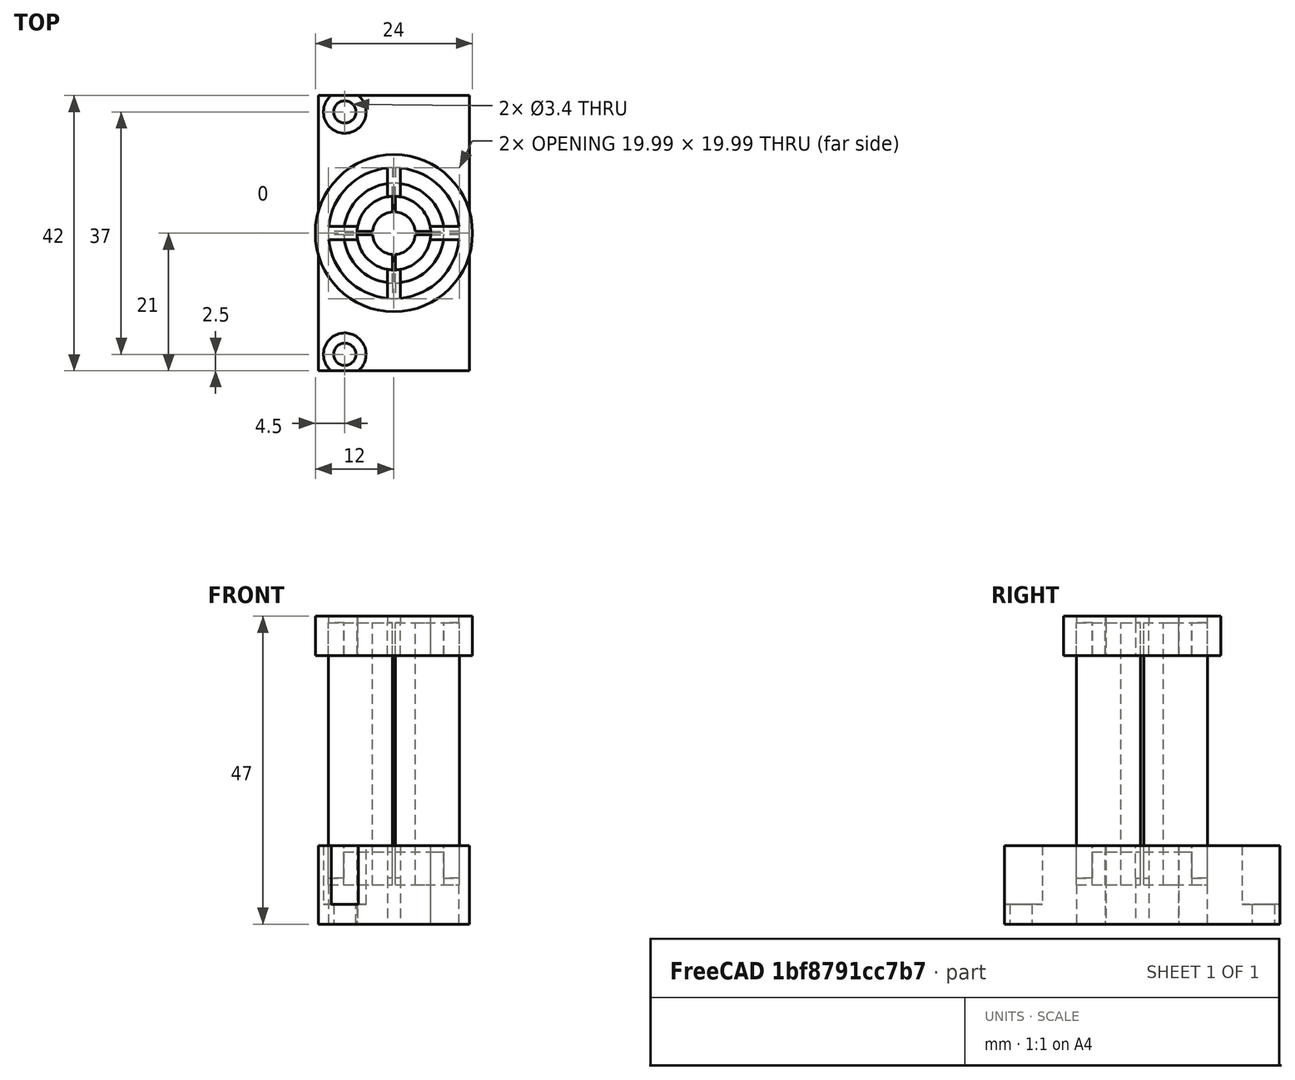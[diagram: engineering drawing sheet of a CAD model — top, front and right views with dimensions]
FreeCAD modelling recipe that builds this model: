
FCSTD DOCUMENT  (FreeCAD 1.0R1.0.0)
Label: Quak_XL30_Modulator3
License: All rights reserved
LicenseURL: http://en.wikipedia.org/wiki/All_rights_reserved
objects: Part::Cut×18, Part::FeaturePython×11, Part::Box×11, TechDraw::DrawViewDimension×9, Part::MultiFuse×8, Part::Cylinder×7, Part::Compound×5, TechDraw::DrawProjGroupItem×3, App::Link×1, Spreadsheet::Sheet×1, TechDraw::DrawSVGTemplate×1, TechDraw::DrawViewSection×1, TechDraw::DrawPage×1
note: 71 computed .brp shape members not serialized (recipe doc carries the construction recipe); baked Part::Feature solids carry a one-line shape summary decoded from their .brp
EXTERNAL_REF file=XL30ColumnAttachmentRing_PCBKicker01.FCStd obj=Cut007

FEATURE [App::Link] Link  label="Stackmountring02"
  LinkedObject = -> <external XL30ColumnAttachmentRing_PCBKicker01.FCStd>#Cut007
FEATURE [Part::FeaturePython] Tube  # WARN: FeaturePython — macro-defined, semantics opaque (R4)
  AttacherType = Attacher::AttachEngine3D
  Height = 40
  InnerRadius = 3.25
  OuterRadius = 10
  expr: Height = <<Modulator3>>.kicker_length
  expr: InnerRadius = <<Modulator3>>.beamhole_diameter / 2
  expr: OuterRadius = <<Modulator3>>.outer_dia / 2
FEATURE [Spreadsheet::Sheet] Spreadsheet  label="Modulator3"
  cells = A2='Beamhole diameter; B2(beamhole_diameter)=6.5; A3='Insulation spacing; B3(insulation_spacing)=0.5; A4='Kicker length; B4(kicker_length)=40; A5='Outer diameter; B5(outer_dia)=20; A6='Shielding plate thickness; B6(shield_thickness)=1; A7='Kicker plate offset; B7(kicker_plate_offset)=7; A8='Mountring diameter; B8(mountring_dia)=2; A9='Mountring depth; B9(mountring_depth)=5; A10='PLA mount (pressfit); A11='Thickness; B11(mount_thickness_bottom)=5; A12='Thickness top; B12(mount_thickness_top)=2
FEATURE [Part::Box] Box  label="Cube"
  AttacherType = Attacher::AttachEngine3D
  Height = 40
  Length = 20
  Placement = pos=(-10,-0.25,0) rot=(0,0,1;0rad)
  Width = 0.5
  expr: .Placement.Base.x = -<<Modulator3>>.outer_dia / 2
  expr: .Placement.Base.y = -<<Modulator3>>.insulation_spacing / 2
  expr: Height = <<Modulator3>>.kicker_length
  expr: Length = <<Modulator3>>.outer_dia
  expr: Width = <<Modulator3>>.insulation_spacing
FEATURE [Part::Box] Box001  label="Cube001"
  AttacherType = Attacher::AttachEngine3D
  Height = 40
  Length = 20
  Placement = pos=(-10,-0.25,0) rot=(0,0,1;0rad)
  Width = 0.5
  expr: .Placement.Base.x = -<<Modulator3>>.outer_dia / 2
  expr: .Placement.Base.y = -<<Modulator3>>.insulation_spacing / 2
  expr: Height = <<Modulator3>>.kicker_length
  expr: Length = <<Modulator3>>.outer_dia
  expr: Width = <<Modulator3>>.insulation_spacing
FEATURE [Part::Compound] Compound
  Links = -> [Box001]
  Placement = pos=(0,0,0) rot=(0,0,1;1.5708rad)
FEATURE [Part::MultiFuse] Fusion
  Shapes = -> [Compound,Box]
FEATURE [Part::Cut] Cut
  Base = -> Tube
  Tool = -> Fusion
FEATURE [Part::FeaturePython] Tube001  label="MountringGroove"  # WARN: FeaturePython — macro-defined, semantics opaque (R4)
  AttacherType = Attacher::AttachEngine3D
  Height = 5
  InnerRadius = 5.625
  OuterRadius = 7.625
  expr: Height = <<Modulator3>>.mountring_depth
  expr: InnerRadius = (<<Modulator3>>.beamhole_diameter + <<Modulator3>>.outer_dia) / 4 - <<Modulator3>>.mountring_dia / 2
  expr: OuterRadius = (<<Modulator3>>.beamhole_diameter + <<Modulator3>>.outer_dia) / 4 + <<Modulator3>>.mountring_dia / 2
FEATURE [Part::Cut] Cut001
  Base = -> Cut
  Tool = -> Tube001
FEATURE [Part::FeaturePython] Tube002  label="MountringGroove001"  # WARN: FeaturePython — macro-defined, semantics opaque (R4)
  AttacherType = Attacher::AttachEngine3D
  Height = 5
  InnerRadius = 5.625
  OuterRadius = 7.625
  Placement = pos=(0,0,35) rot=(0,0,1;0rad)
  expr: .Placement.Base.z = <<Modulator3>>.kicker_length - <<Modulator3>>.mountring_depth
  expr: Height = <<Modulator3>>.mountring_depth
  expr: InnerRadius = (<<Modulator3>>.beamhole_diameter + <<Modulator3>>.outer_dia) / 4 - <<Modulator3>>.mountring_dia / 2
  expr: OuterRadius = (<<Modulator3>>.beamhole_diameter + <<Modulator3>>.outer_dia) / 4 + <<Modulator3>>.mountring_dia / 2
FEATURE [Part::Cut] Cut002  label="ModulatorPlates"
  Base = -> Cut001
  Placement = pos=(0,0,11) rot=(0,0,1;0rad)
  Tool = -> Tube002
FEATURE [Part::Box] Box002  label="Cube002"
  AttacherType = Attacher::AttachEngine3D
  Height = 12
  Length = 23
  Placement = pos=(-11.5,-21,0) rot=(0,0,1;0rad)
  Width = 42
  expr: Height = <<Modulator3>>.mount_thickness_bottom + 7
FEATURE [Part::Cylinder] Cylinder
  Angle = 360
  AttacherType = Attacher::AttachEngine3D
  FirstAngle = 0
  Height = 100
  Radius = 5.625
  SecondAngle = 0
  expr: Radius = (<<Modulator3>>.beamhole_diameter + <<Modulator3>>.outer_dia) / 4 - <<Modulator3>>.mountring_dia / 2
FEATURE [Part::Cut] Cut003
  Base = -> Box002
  Tool = -> Cylinder
FEATURE [Part::Box] Box003  label="Cube003"
  AttacherType = Attacher::AttachEngine3D
  Height = 40
  Length = 20
  Placement = pos=(-10,-0.25,0) rot=(0,0,1;0rad)
  Width = 0.5
  expr: .Placement.Base.x = -<<Modulator3>>.outer_dia / 2
  expr: .Placement.Base.y = -<<Modulator3>>.insulation_spacing / 2
  expr: Height = <<Modulator3>>.kicker_length
  expr: Length = <<Modulator3>>.outer_dia
  expr: Width = <<Modulator3>>.insulation_spacing
FEATURE [Part::Box] Box004  label="Cube004"
  AttacherType = Attacher::AttachEngine3D
  Height = 40
  Length = 20
  Placement = pos=(-10,-0.25,0) rot=(0,0,1;0rad)
  Width = 0.5
  expr: .Placement.Base.x = -<<Modulator3>>.outer_dia / 2
  expr: .Placement.Base.y = -<<Modulator3>>.insulation_spacing / 2
  expr: Height = <<Modulator3>>.kicker_length
  expr: Length = <<Modulator3>>.outer_dia
  expr: Width = <<Modulator3>>.insulation_spacing
FEATURE [Part::Compound] Compound001
  Links = -> [Box004]
  Placement = pos=(0,0,0) rot=(0,0,1;1.5708rad)
FEATURE [Part::MultiFuse] Fusion001
  Shapes = -> [Compound001,Box003]
FEATURE [Part::FeaturePython] Tube003  # WARN: FeaturePython — macro-defined, semantics opaque (R4)
  AttacherType = Attacher::AttachEngine3D
  Height = 40
  InnerRadius = 3.25
  OuterRadius = 10
  expr: Height = <<Modulator3>>.kicker_length
  expr: InnerRadius = <<Modulator3>>.beamhole_diameter / 2
  expr: OuterRadius = <<Modulator3>>.outer_dia / 2
FEATURE [Part::Cut] Cut004
  Base = -> Tube003
  Tool = -> Fusion001
FEATURE [Part::FeaturePython] Tube004  label="MountringGroove002"  # WARN: FeaturePython — macro-defined, semantics opaque (R4)
  AttacherType = Attacher::AttachEngine3D
  Height = 5
  InnerRadius = 5.625
  OuterRadius = 7.625
  expr: Height = <<Modulator3>>.mountring_depth
  expr: InnerRadius = (<<Modulator3>>.beamhole_diameter + <<Modulator3>>.outer_dia) / 4 - <<Modulator3>>.mountring_dia / 2
  expr: OuterRadius = (<<Modulator3>>.beamhole_diameter + <<Modulator3>>.outer_dia) / 4 + <<Modulator3>>.mountring_dia / 2
FEATURE [Part::Cut] Cut005
  Base = -> Cut004
  Tool = -> Tube004
FEATURE [Part::FeaturePython] Tube005  label="MountringGroove003"  # WARN: FeaturePython — macro-defined, semantics opaque (R4)
  AttacherType = Attacher::AttachEngine3D
  Height = 5
  InnerRadius = 5.625
  OuterRadius = 7.625
  Placement = pos=(0,0,35) rot=(0,0,1;0rad)
  expr: .Placement.Base.z = <<Modulator3>>.kicker_length - <<Modulator3>>.mountring_depth
  expr: Height = <<Modulator3>>.mountring_depth
  expr: InnerRadius = (<<Modulator3>>.beamhole_diameter + <<Modulator3>>.outer_dia) / 4 - <<Modulator3>>.mountring_dia / 2
  expr: OuterRadius = (<<Modulator3>>.beamhole_diameter + <<Modulator3>>.outer_dia) / 4 + <<Modulator3>>.mountring_dia / 2
FEATURE [Part::Cut] Cut006
  Base = -> Cut005
  Placement = pos=(0,0,7) rot=(0,0,1;0rad)
  Tool = -> Tube005
FEATURE [Part::Cut] Cut007
  Base = -> Cut003
  Placement = pos=(0,0,1) rot=(0,0,1;0rad)
  Tool = -> Cut006
FEATURE [Part::Cylinder] Cylinder001
  Angle = 360
  AttacherType = Attacher::AttachEngine3D
  FirstAngle = 0
  Height = 6
  Placement = pos=(0,0,42) rot=(0,0,1;0rad)
  Radius = 12
  SecondAngle = 0
  expr: .Placement.Base.z = <<Modulator3>>.kicker_length + 7 - <<Modulator3>>.mountring_depth
  expr: Height = <<Modulator3>>.mountring_depth + 1
  expr: Radius = <<Modulator3>>.outer_dia / 2 + 2
FEATURE [Part::Cylinder] Cylinder002
  Angle = 360
  AttacherType = Attacher::AttachEngine3D
  FirstAngle = 0
  Height = 100
  Radius = 5.625
  SecondAngle = 0
  expr: Radius = (<<Modulator3>>.beamhole_diameter + <<Modulator3>>.outer_dia) / 4 - <<Modulator3>>.mountring_dia / 2
FEATURE [Part::Cut] Cut008
  Base = -> Cylinder001
  Tool = -> Cylinder002
FEATURE [Part::Box] Box005  label="Cube005"
  AttacherType = Attacher::AttachEngine3D
  Height = 40
  Length = 20
  Placement = pos=(-10,-0.25,0) rot=(0,0,1;0rad)
  Width = 0.5
  expr: .Placement.Base.x = -<<Modulator3>>.outer_dia / 2
  expr: .Placement.Base.y = -<<Modulator3>>.insulation_spacing / 2
  expr: Height = <<Modulator3>>.kicker_length
  expr: Length = <<Modulator3>>.outer_dia
  expr: Width = <<Modulator3>>.insulation_spacing
FEATURE [Part::Box] Box006  label="Cube006"
  AttacherType = Attacher::AttachEngine3D
  Height = 40
  Length = 20
  Placement = pos=(-10,-0.25,0) rot=(0,0,1;0rad)
  Width = 0.5
  expr: .Placement.Base.x = -<<Modulator3>>.outer_dia / 2
  expr: .Placement.Base.y = -<<Modulator3>>.insulation_spacing / 2
  expr: Height = <<Modulator3>>.kicker_length
  expr: Length = <<Modulator3>>.outer_dia
  expr: Width = <<Modulator3>>.insulation_spacing
FEATURE [Part::Compound] Compound002
  Links = -> [Box006]
  Placement = pos=(0,0,0) rot=(0,0,1;1.5708rad)
FEATURE [Part::MultiFuse] Fusion002
  Shapes = -> [Compound002,Box005]
FEATURE [Part::FeaturePython] Tube006  # WARN: FeaturePython — macro-defined, semantics opaque (R4)
  AttacherType = Attacher::AttachEngine3D
  Height = 40
  InnerRadius = 3.25
  OuterRadius = 10
  expr: Height = <<Modulator3>>.kicker_length
  expr: InnerRadius = <<Modulator3>>.beamhole_diameter / 2
  expr: OuterRadius = <<Modulator3>>.outer_dia / 2
FEATURE [Part::Cut] Cut009
  Base = -> Tube006
  Tool = -> Fusion002
FEATURE [Part::FeaturePython] Tube007  label="MountringGroove004"  # WARN: FeaturePython — macro-defined, semantics opaque (R4)
  AttacherType = Attacher::AttachEngine3D
  Height = 5
  InnerRadius = 5.625
  OuterRadius = 7.625
  expr: Height = <<Modulator3>>.mountring_depth
  expr: InnerRadius = (<<Modulator3>>.beamhole_diameter + <<Modulator3>>.outer_dia) / 4 - <<Modulator3>>.mountring_dia / 2
  expr: OuterRadius = (<<Modulator3>>.beamhole_diameter + <<Modulator3>>.outer_dia) / 4 + <<Modulator3>>.mountring_dia / 2
FEATURE [Part::Cut] Cut010
  Base = -> Cut009
  Tool = -> Tube007
FEATURE [Part::FeaturePython] Tube008  label="MountringGroove005"  # WARN: FeaturePython — macro-defined, semantics opaque (R4)
  AttacherType = Attacher::AttachEngine3D
  Height = 5
  InnerRadius = 5.625
  OuterRadius = 7.625
  Placement = pos=(0,0,35) rot=(0,0,1;0rad)
  expr: .Placement.Base.z = <<Modulator3>>.kicker_length - <<Modulator3>>.mountring_depth
  expr: Height = <<Modulator3>>.mountring_depth
  expr: InnerRadius = (<<Modulator3>>.beamhole_diameter + <<Modulator3>>.outer_dia) / 4 - <<Modulator3>>.mountring_dia / 2
  expr: OuterRadius = (<<Modulator3>>.beamhole_diameter + <<Modulator3>>.outer_dia) / 4 + <<Modulator3>>.mountring_dia / 2
FEATURE [Part::Cut] Cut011
  Base = -> Cut010
  Placement = pos=(0,0,7) rot=(0,0,1;0rad)
  Tool = -> Tube008
FEATURE [Part::Cut] Cut012  label="mountring_top"
  Base = -> Cut008
  Placement = pos=(0,0,4) rot=(0,0,1;0rad)
  Tool = -> Cut011
FEATURE [Part::Cylinder] Cylinder003
  Angle = 360
  AttacherType = Attacher::AttachEngine3D
  FirstAngle = 0
  Height = 12
  Radius = 1.7
  SecondAngle = 0
  expr: Height = <<Modulator3>>.mount_thickness_bottom + 7
FEATURE [Part::Cylinder] Cylinder004
  Angle = 360
  AttacherType = Attacher::AttachEngine3D
  FirstAngle = 0
  Height = 9
  Placement = pos=(0,0,3) rot=(0,0,1;0rad)
  Radius = 3.25
  SecondAngle = 0
  expr: Height = <<Modulator3>>.mount_thickness_bottom + 7 - 3
  expr: Radius = 3.25 mm
FEATURE [Part::MultiFuse] Fusion003
  Placement = pos=(-7.5,18.5,0) rot=(0,0,1;0rad)
  Shapes = -> [Cylinder004,Cylinder003]
FEATURE [Part::Cylinder] Cylinder005
  Angle = 360
  AttacherType = Attacher::AttachEngine3D
  FirstAngle = 0
  Height = 12
  Radius = 1.7
  SecondAngle = 0
  expr: Height = <<Modulator3>>.mount_thickness_bottom + 7
FEATURE [Part::Cylinder] Cylinder006
  Angle = 360
  AttacherType = Attacher::AttachEngine3D
  FirstAngle = 0
  Height = 9
  Placement = pos=(0,0,3) rot=(0,0,1;0rad)
  Radius = 3.25
  SecondAngle = 0
  expr: Height = <<Modulator3>>.mount_thickness_bottom + 7 - 3
  expr: Radius = 3.25 mm
FEATURE [Part::MultiFuse] Fusion004
  Placement = pos=(-7.5,-18.5,0) rot=(0,0,1;0rad)
  Shapes = -> [Cylinder006,Cylinder005]
  expr: .Placement.Base.y = -18.5 mm
FEATURE [Part::MultiFuse] Fusion005
  Placement = pos=(0,0,1) rot=(0,0,1;0rad)
  Shapes = -> [Fusion004,Fusion003]
FEATURE [Part::Cut] Cut013
  Base = -> Cut007
  Placement = pos=(0,0,4) rot=(0,0,1;0rad)
  Tool = -> Fusion005
FEATURE [Part::Box] Box009  label="Cube009"
  AttacherType = Attacher::AttachEngine3D
  Height = 80
  Length = 20
  Placement = pos=(-10,-1,-20) rot=(0,0,1;0rad)
  Width = 2
  expr: .Placement.Base.x = -<<Modulator3>>.outer_dia / 2
  expr: .Placement.Base.y = -(<<Modulator3>>.insulation_spacing * 4) / 2
  expr: .Placement.Base.z = -<<Modulator3>>.kicker_length / 2
  expr: Height = <<Modulator3>>.kicker_length * 2
  expr: Length = <<Modulator3>>.outer_dia
  expr: Width = <<Modulator3>>.insulation_spacing * 4
FEATURE [Part::Box] Box010  label="Cube010"
  AttacherType = Attacher::AttachEngine3D
  Height = 80
  Length = 20
  Placement = pos=(-10,-1,-20) rot=(0,0,1;0rad)
  Width = 2
  expr: .Placement.Base.x = -<<Modulator3>>.outer_dia / 2
  expr: .Placement.Base.y = -(<<Modulator3>>.insulation_spacing * 4) / 2
  expr: .Placement.Base.z = -<<Modulator3>>.kicker_length / 2
  expr: Height = <<Modulator3>>.kicker_length * 2
  expr: Length = <<Modulator3>>.outer_dia
  expr: Width = <<Modulator3>>.insulation_spacing * 4
FEATURE [Part::Compound] Compound004
  Links = -> [Box010]
  Placement = pos=(0,0,0) rot=(0,0,1;1.5708rad)
FEATURE [Part::MultiFuse] Fusion007
  Shapes = -> [Compound004,Box009]
FEATURE [Part::FeaturePython] Tube012  # WARN: FeaturePython — macro-defined, semantics opaque (R4)
  AttacherType = Attacher::AttachEngine3D
  Height = 80
  InnerRadius = 3.25
  OuterRadius = 10
  Placement = pos=(0,0,-20) rot=(0,0,1;0rad)
  expr: .Placement.Base.z = -<<Modulator3>>.kicker_length / 2
  expr: Height = <<Modulator3>>.kicker_length * 2
  expr: InnerRadius = <<Modulator3>>.beamhole_diameter / 2
  expr: OuterRadius = <<Modulator3>>.outer_dia / 2
FEATURE [Part::Cut] Cut017
  Base = -> Tube012
  Tool = -> Fusion007
FEATURE [Part::Box] Box011  label="Cube011"
  AttacherType = Attacher::AttachEngine3D
  Height = 80
  Length = 20
  Placement = pos=(-10,-1,-20) rot=(0,0,1;0rad)
  Width = 2
  expr: .Placement.Base.x = -<<Modulator3>>.outer_dia / 2
  expr: .Placement.Base.y = -(<<Modulator3>>.insulation_spacing * 4) / 2
  expr: .Placement.Base.z = -<<Modulator3>>.kicker_length / 2
  expr: Height = <<Modulator3>>.kicker_length * 2
  expr: Length = <<Modulator3>>.outer_dia
  expr: Width = <<Modulator3>>.insulation_spacing * 4
FEATURE [Part::Box] Box012  label="Cube012"
  AttacherType = Attacher::AttachEngine3D
  Height = 80
  Length = 20
  Placement = pos=(-10,-1,-20) rot=(0,0,1;0rad)
  Width = 2
  expr: .Placement.Base.x = -<<Modulator3>>.outer_dia / 2
  expr: .Placement.Base.y = -(<<Modulator3>>.insulation_spacing * 4) / 2
  expr: .Placement.Base.z = -<<Modulator3>>.kicker_length / 2
  expr: Height = <<Modulator3>>.kicker_length * 2
  expr: Length = <<Modulator3>>.outer_dia
  expr: Width = <<Modulator3>>.insulation_spacing * 4
FEATURE [Part::Compound] Compound005
  Links = -> [Box012]
  Placement = pos=(0,0,0) rot=(0,0,1;1.5708rad)
FEATURE [Part::MultiFuse] Fusion008
  Shapes = -> [Compound005,Box011]
FEATURE [Part::FeaturePython] Tube013  # WARN: FeaturePython — macro-defined, semantics opaque (R4)
  AttacherType = Attacher::AttachEngine3D
  Height = 80
  InnerRadius = 3.25
  OuterRadius = 10
  Placement = pos=(0,0,-20) rot=(0,0,1;0rad)
  expr: .Placement.Base.z = -<<Modulator3>>.kicker_length / 2
  expr: Height = <<Modulator3>>.kicker_length * 2
  expr: InnerRadius = <<Modulator3>>.beamhole_diameter / 2
  expr: OuterRadius = <<Modulator3>>.outer_dia / 2
FEATURE [Part::Cut] Cut018
  Base = -> Tube013
  Tool = -> Fusion008
FEATURE [Part::Cut] Cut019  label="TopRing"
  Base = -> Cut012
  Tool = -> Cut018
FEATURE [Part::Cut] Cut020  label="BottomMount"
  Base = -> Cut013
  Tool = -> Cut017
FEATURE [TechDraw::DrawSVGTemplate] Template
  EditableTexts = creator=Thomas Spielauer; date_of_issue=2 Apr 2025; document_type=Part Drawing; general_tolerances=ISO 2768-m; identification_number=1; language_code=EN; part_material=Copper; revision_index=1; sheet_number=1 / 1; sheet_scale=1 : 1; title=Circular Modulator Plates
  Height = 210
  Orientation = 1
  Template = <path>
  Width = 297
FEATURE [TechDraw::DrawProjGroupItem] View
  CoarseView = false
  Direction = (0,-1,0)
  Focus = 100
  HardHidden = false
  IsoCount = 0
  IsoHidden = false
  IsoVisible = false
  LockPosition = false
  Perspective = false
  Rotation = 0
  RotationVector = (1,0,0)
  Scale = 2
  ScaleType = 2
  ScrubCount = 1
  SeamHidden = false
  SeamVisible = false
  SmoothHidden = false
  SmoothVisible = true
  Source = -> [Cut002]
  Type = 0
  X = 51.9109
  XDirection = (1,0,0)
  Y = 139.65
FEATURE [TechDraw::DrawProjGroupItem] View001
  CoarseView = false
  Direction = (0,0,1)
  Focus = 100
  HardHidden = false
  IsoCount = 0
  IsoHidden = false
  IsoVisible = false
  LockPosition = false
  Perspective = false
  Rotation = 0
  RotationVector = (1,0,0)
  Scale = 3
  ScaleType = 2
  ScrubCount = 1
  SeamHidden = false
  SeamVisible = false
  SmoothHidden = false
  SmoothVisible = true
  Source = -> [Cut002]
  Type = 0
  X = 116.051
  XDirection = (1,0,0)
  Y = 139.65
FEATURE [TechDraw::DrawViewSection] SectionView  label="Section  - "
  BaseView = -> View001
  CoarseView = false
  CutSurfaceDisplay = 2
  Direction = (-1,-1e-16,0)
  FileGeomPattern = <path>
  FileHatchPattern = <path>
  Focus = 100
  FuseBeforeCut = false
  HardHidden = false
  HatchOffset = (0,0,0)
  HatchRotation = 0
  HatchScale = 1
  IsoCount = 0
  IsoHidden = false
  IsoVisible = false
  LockPosition = false
  NameGeomPattern = Diamond
  Perspective = false
  Rotation = -90
  Scale = 3
  ScaleType = 2
  ScrubCount = 1
  SeamHidden = false
  SeamVisible = false
  SectionDirection = 4
  SectionLineStretch = 1
  SectionNormal = (-1,-1e-16,0)
  SectionOrigin = (0,0,31)
  SmoothHidden = false
  SmoothVisible = true
  Source = -> [Cut002]
  TrimAfterCut = false
  UsePreviousCut = false
  X = 219.773
  XDirection = (1e-16,-1,0)
  Y = 139.65
FEATURE [TechDraw::DrawProjGroupItem] View002
  CoarseView = false
  Direction = (-0.57735,0.57735,0.57735)
  Focus = 100
  HardHidden = false
  IsoCount = 0
  IsoHidden = false
  IsoVisible = false
  LockPosition = false
  Perspective = false
  Rotation = 0
  RotationVector = (1,0,0)
  ScaleType = 0
  ScrubCount = 1
  SeamHidden = false
  SeamVisible = false
  SmoothHidden = false
  SmoothVisible = true
  Source = -> [Cut002]
  Type = 0
  X = 58.6848
  XDirection = (-0.816496,-0.408248,-0.408248)
  Y = 44.7369
FEATURE [TechDraw::DrawViewDimension] Dimension
  AngleOverride = false
  Arbitrary = false
  ArbitraryTolerances = false
  BoxCorners = (2) [(-19.9937,-40,-1e-07),(19.9937,40,1e-07)]
  EqualTolerance = true
  ExtensionAngle = 0
  FormatSpec = %.2w
  FormatSpecOverTolerance = %+.2w
  FormatSpecUnderTolerance = %+.2w
  Inverted = false
  LineAngle = 0
  LockPosition = false
  MeasureType = 1
  OverTolerance = 0
  References2D = -> [View]
  Rotation = 0
  ScaleType = 0
  TheoreticalExact = false
  Type = 2
  UnderTolerance = 0
  X = -28.5041
  Y = 5.24359
FEATURE [TechDraw::DrawViewDimension] Dimension001
  AngleOverride = false
  Arbitrary = false
  ArbitraryTolerances = false
  BoxCorners = (2) [(-29.9906,-29.9906,0),(29.9906,29.9906,0)]
  EqualTolerance = true
  ExtensionAngle = 0
  FormatSpec = ⌀%.2w
  FormatSpecOverTolerance = %+.2w
  FormatSpecUnderTolerance = %+.2w
  Inverted = false
  LineAngle = 0
  LockPosition = false
  MeasureType = 1
  OverTolerance = 0
  References2D = -> [View001]
  Rotation = 0
  ScaleType = 0
  TheoreticalExact = false
  Type = 5
  UnderTolerance = 0
  X = -33.5321
  Y = 32.1098
FEATURE [TechDraw::DrawViewDimension] Dimension002
  AngleOverride = false
  Arbitrary = false
  ArbitraryTolerances = false
  BoxCorners = (2) [(-29.9906,-29.9906,0),(29.9906,29.9906,0)]
  EqualTolerance = true
  ExtensionAngle = 0
  FormatSpec = ⌀%.2w
  FormatSpecOverTolerance = %+.2w
  FormatSpecUnderTolerance = %+.2w
  Inverted = false
  LineAngle = 0
  LockPosition = false
  MeasureType = 1
  OverTolerance = 0
  References2D = -> [View001]
  Rotation = 0
  ScaleType = 0
  TheoreticalExact = false
  Type = 5
  UnderTolerance = 0
  X = -26.99
  Y = 39.9471
FEATURE [TechDraw::DrawViewDimension] Dimension003
  AngleOverride = false
  Arbitrary = false
  ArbitraryTolerances = false
  BoxCorners = (2) [(-29.9906,-29.9906,0),(29.9906,29.9906,0)]
  EqualTolerance = true
  ExtensionAngle = 0
  FormatSpec = ⌀%.2w
  FormatSpecOverTolerance = %+.2w
  FormatSpecUnderTolerance = %+.2w
  Inverted = false
  LineAngle = 0
  LockPosition = false
  MeasureType = 1
  OverTolerance = 0
  References2D = -> [View001]
  Rotation = 0
  ScaleType = 0
  TheoreticalExact = false
  Type = 5
  UnderTolerance = 0
  X = -19.0316
  Y = 46.4094
FEATURE [TechDraw::DrawViewDimension] Dimension004
  AngleOverride = false
  Arbitrary = false
  ArbitraryTolerances = false
  BoxCorners = (2) [(-29.9906,-29.9906,0),(29.9906,29.9906,0)]
  EqualTolerance = true
  ExtensionAngle = 0
  FormatSpec = ⌀%.2w
  FormatSpecOverTolerance = %+.2w
  FormatSpecUnderTolerance = %+.2w
  Inverted = false
  LineAngle = 0
  LockPosition = false
  MeasureType = 1
  OverTolerance = 0
  References2D = -> [View001]
  Rotation = 0
  ScaleType = 0
  TheoreticalExact = false
  Type = 5
  UnderTolerance = 0
  X = -9.58678
  Y = 48.0562
FEATURE [TechDraw::DrawViewDimension] Dimension005
  AngleOverride = false
  Arbitrary = false
  ArbitraryTolerances = false
  BoxCorners = (2) [(-60,-29.9906,-1e-07),(60,29.9906,1e-07)]
  EqualTolerance = true
  ExtensionAngle = 0
  FormatSpec = %.2w
  FormatSpecOverTolerance = %+.2w
  FormatSpecUnderTolerance = %+.2w
  Inverted = false
  LineAngle = 0
  LockPosition = false
  MeasureType = 1
  OverTolerance = 0
  References2D = -> [SectionView]
  Rotation = 0
  ScaleType = 0
  TheoreticalExact = false
  Type = 1
  UnderTolerance = 0
  X = 0
  Y = 45.3048
FEATURE [TechDraw::DrawViewDimension] Dimension006
  AngleOverride = false
  Arbitrary = false
  ArbitraryTolerances = false
  BoxCorners = (2) [(-60,-29.9906,-1e-07),(60,29.9906,1e-07)]
  EqualTolerance = true
  ExtensionAngle = 0
  FormatSpec = %.2w
  FormatSpecOverTolerance = %+.2w
  FormatSpecUnderTolerance = %+.2w
  Inverted = false
  LineAngle = 0
  LockPosition = false
  MeasureType = 1
  OverTolerance = 0
  References2D = -> [SectionView]
  Rotation = 0
  ScaleType = 0
  TheoreticalExact = false
  Type = 1
  UnderTolerance = 0
  X = -52.5
  Y = 38.3048
FEATURE [TechDraw::DrawViewDimension] Dimension007
  AngleOverride = false
  Arbitrary = false
  ArbitraryTolerances = false
  BoxCorners = (2) [(-60,-29.9906,-1e-07),(60,29.9906,1e-07)]
  EqualTolerance = true
  ExtensionAngle = 0
  FormatSpec = %.2w
  FormatSpecOverTolerance = %+.2w
  FormatSpecUnderTolerance = %+.2w
  Inverted = false
  LineAngle = 0
  LockPosition = false
  MeasureType = 1
  OverTolerance = 0
  References2D = -> [SectionView]
  Rotation = 0
  ScaleType = 0
  TheoreticalExact = false
  Type = 2
  UnderTolerance = 0
  X = -33.8378
  Y = 19.8605
FEATURE [TechDraw::DrawViewDimension] Dimension008
  AngleOverride = false
  Arbitrary = false
  ArbitraryTolerances = false
  BoxCorners = (2) [(-29.9906,-29.9906,0),(29.9906,29.9906,0)]
  EqualTolerance = true
  ExtensionAngle = 0
  FormatSpec = %.2w
  FormatSpecOverTolerance = %+.2w
  FormatSpecUnderTolerance = %+.2w
  Inverted = false
  LineAngle = 0
  LockPosition = false
  MeasureType = 1
  OverTolerance = 0
  References2D = -> [View001]
  Rotation = 0
  ScaleType = 0
  TheoreticalExact = false
  Type = 2
  UnderTolerance = 0
  X = 32.8092
  Y = 9.68928
FEATURE [TechDraw::DrawPage] Page
  KeepUpdated = true
  NextBalloonIndex = 1
  ProjectionType = 0
  Template = -> Template
  Views = -> [View,View001,SectionView,View002,Dimension,Dimension001,Dimension002,Dimension003,Dimension004,Dimension005,Dimension006,Dimension007,Dimension008]
note: 3 file-system paths scrubbed to <path> (originals preserved in the JSON sidecar)
